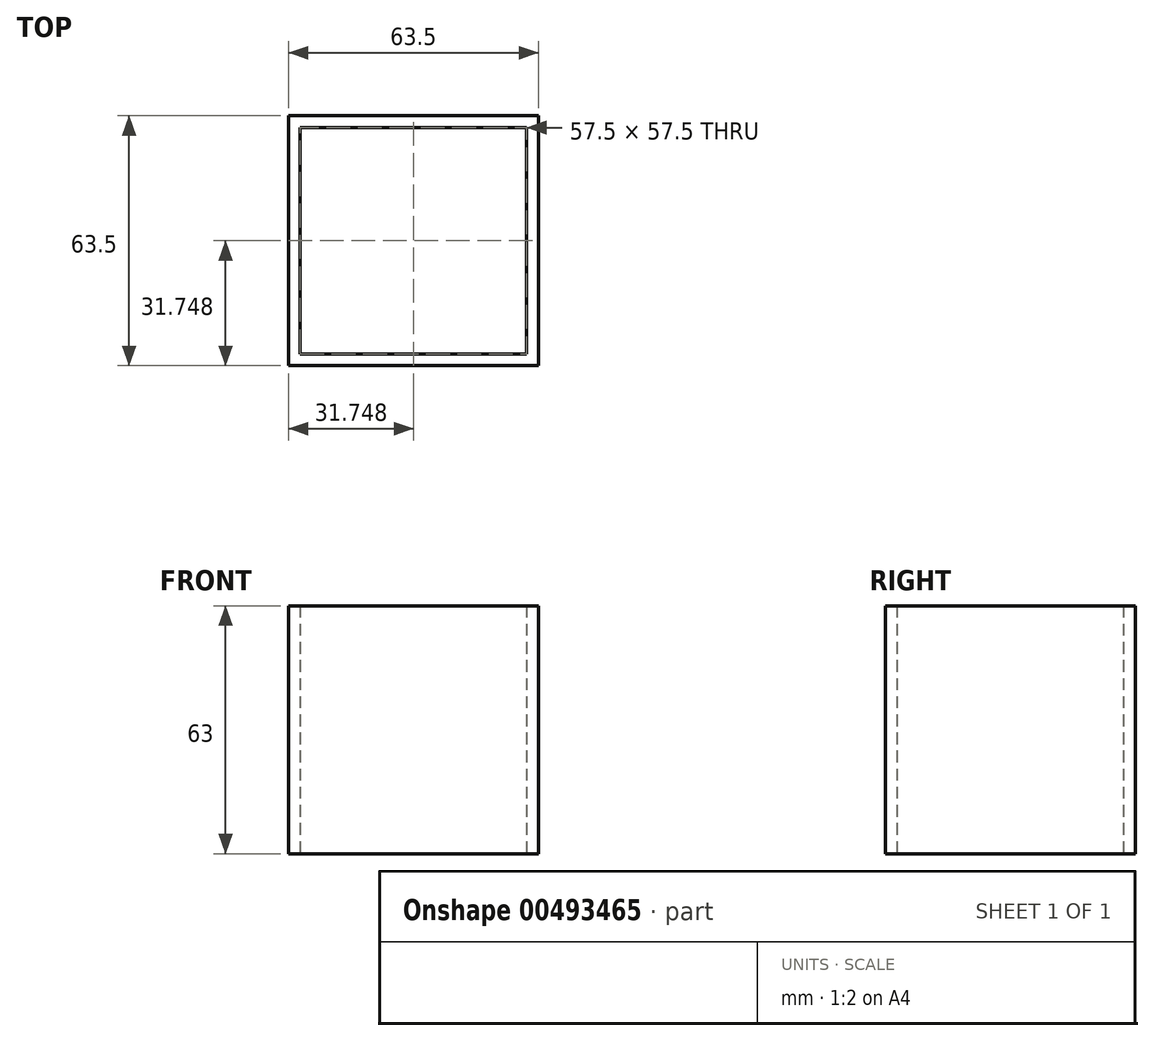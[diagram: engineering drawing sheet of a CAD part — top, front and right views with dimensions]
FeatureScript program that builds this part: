
annotation { "Feature Type Name" : "Feature", "Feature Type Description" : "" }
export const myFeature = defineFeature(function(context is Context, id is Id, definition is map)
    precondition{}
    {
        {
            var Q0;
            Q0=qCreatedBy(makeId("Top.planeOp"),FACE);
            var sketch = newSketch(context, id + "F0", { "sketchPlane" : qUnion([Q0])});
            skLineSegment(sketch, "E0.bottom", {"start": v(-24.28, 32.34) * mm, "end": v(33.22, 32.34) * mm});
            skLineSegment(sketch, "E0.top", {"start": v(-24.28, -25.16) * mm, "end": v(33.22, -25.16) * mm});
            skLineSegment(sketch, "E0.left", {"start": v(-24.28, 32.34) * mm, "end": v(-24.28, -25.16) * mm});
            skLineSegment(sketch, "E0.right", {"start": v(33.22, 32.34) * mm, "end": v(33.22, -25.16) * mm});
            skLineSegment(sketch, "E1.bottom", {"start": v(-27.28, 35.34) * mm, "end": v(36.22, 35.34) * mm});
            skLineSegment(sketch, "E1.top", {"start": v(-27.28, -28.16) * mm, "end": v(36.22, -28.16) * mm});
            skLineSegment(sketch, "E1.left", {"start": v(-27.28, 35.34) * mm, "end": v(-27.28, -28.16) * mm});
            skLineSegment(sketch, "E1.right", {"start": v(36.22, 35.34) * mm, "end": v(36.22, -28.16) * mm});
            skSolve(sketch);
        }
        {
            var Q0;
            Q0 = qSketchRegion(id + "F0", true);
            extrude(context, id + "F1", {"entities" : qUnion([Q0]), "depth" : 63 * mm});
        }
    });
